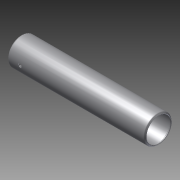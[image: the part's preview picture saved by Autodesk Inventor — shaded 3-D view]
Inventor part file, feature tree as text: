
AUTODESK INVENTOR PART (.ipt)
format: ipt  version: 2012 (Build 160160000, 160)  size: 137,728 bytes
history: native  units: in
note: dims shown in document units (in); Inventor stores cm internally (conversion verified against a paired STEP export)
features: other x42, sketch x2, revolve x1, extrude x1
ambient origin geometry x8: Origin, YZ Plane, XZ Plane, XY Plane, X Axis, Y Axis, Z Axis, Center Point
bodies: Solid1 (feature_tree)
feature tree (46):
  revolve  "Revolution1"  [1 undecoded]
  extrude  "Extrusion1"  [1 undecoded]
  other  "tube_front_XY"
  other  "tube_front_YZ"
  other  "tube_front_ZX"
  other  "tube_front_X"
  other  "tube_front_Y"
  other  "tube_front_Z"
  other  "tube_front_Center"
  other  "tube_rear_XY"
  other  "tube_rear_YZ"
  other  "tube_rear_ZX"
  other  "tube_rear_X"
  other  "tube_rear_Y"
  other  "tube_rear_Z"
  other  "tube_rear_Center"
  other  "cp1_XY"
  other  "cp1_YZ"
  other  "cp1_ZX"
  other  "cp1_X"
  other  "cp1_Y"
  other  "cp1_Z"
  other  "cp1_Center"
  other  "cp2_XY"
  other  "cp2_YZ"
  other  "cp2_ZX"
  other  "cp2_X"
  other  "cp2_Y"
  other  "cp2_Z"
  other  "cp2_Center"
  other  "cp3_XY"
  other  "cp3_YZ"
  other  "cp3_ZX"
  other  "cp3_X"
  other  "cp3_Y"
  other  "cp3_Z"
  other  "cp3_Center"
  other  "cp4_XY"
  other  "cp4_YZ"
  other  "cp4_ZX"
  other  "cp4_X"
  other  "cp4_Y"
  other  "cp4_Z"
  other  "cp4_Center"
  sketch  "Sketch_1"  dims[d0=360.0deg d1=0.4025in d2=0.0in]
  sketch  "Sketch_4"
note: 2 required parameter values undecoded (feature->parameter linkage not recoverable at this tier; creation-order binding heuristic only, values carry confidence <= 0.55)